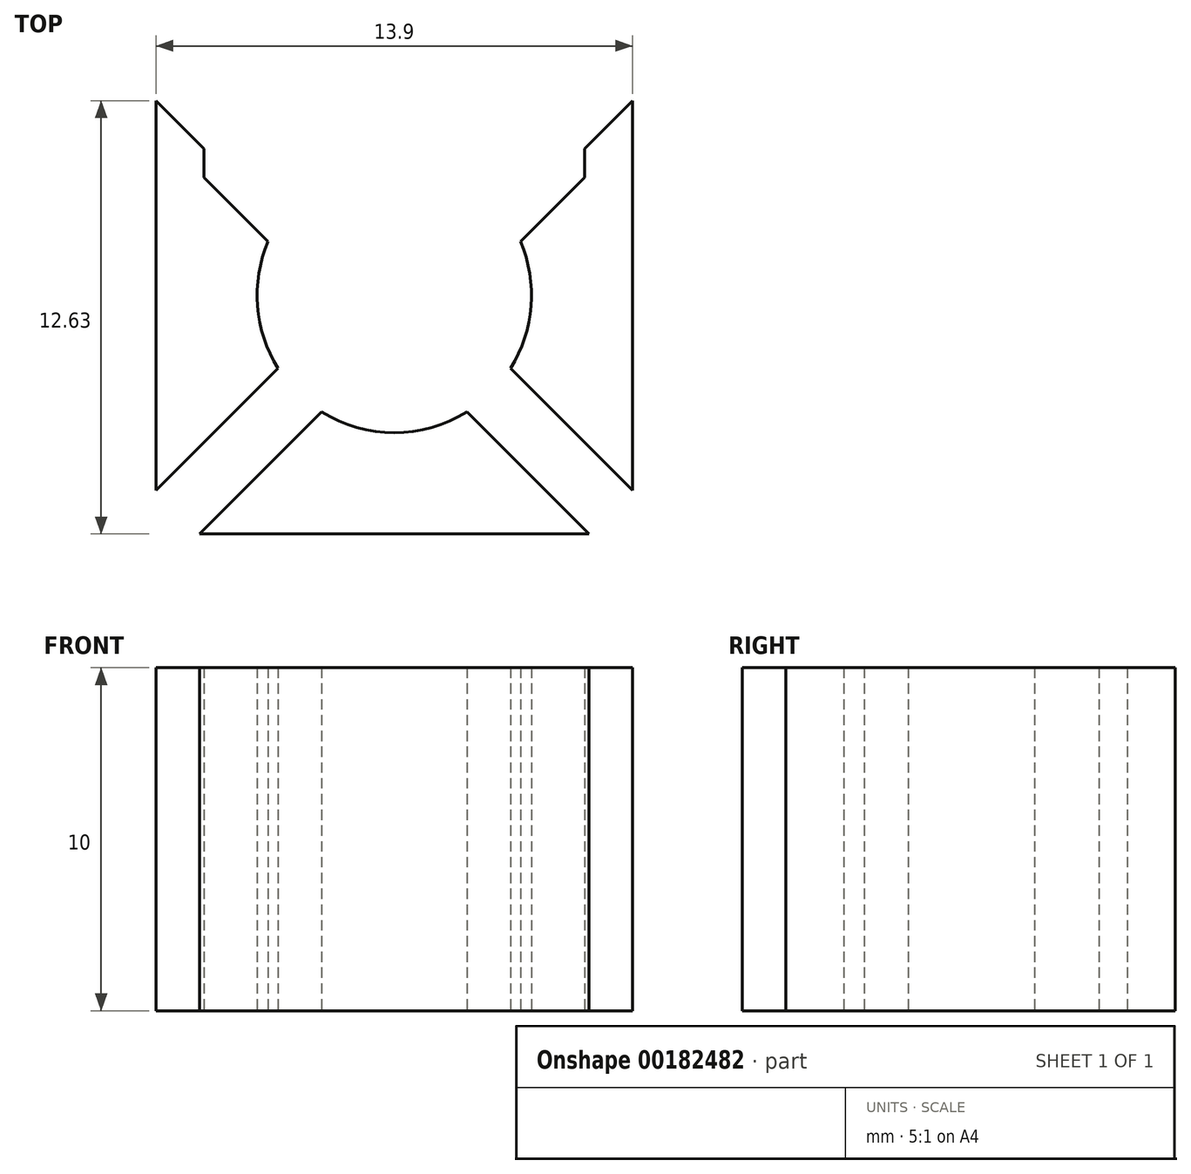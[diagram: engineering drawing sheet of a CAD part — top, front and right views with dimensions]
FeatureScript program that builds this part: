
annotation { "Feature Type Name" : "Feature", "Feature Type Description" : "" }
export const myFeature = defineFeature(function(context is Context, id is Id, definition is map)
    precondition{}
    {
        {
            var Q0;
            Q0=qCreatedBy(makeId("Top.planeOp"),FACE);
            var sketch = newSketch(context, id + "F0", { "sketchPlane" : qUnion([Q0])});
            skLineSegment(sketch, "E0.bottom", {"start": v(8.25, 8.25) * mm, "end": v(-8.25, 8.25) * mm});
            skLineSegment(sketch, "E0.top", {"start": v(8.25, -8.25) * mm, "end": v(-8.25, -8.25) * mm});
            skLineSegment(sketch, "E0.left", {"start": v(8.25, 8.25) * mm, "end": v(8.25, -8.25) * mm});
            skLineSegment(sketch, "E0.right", {"start": v(-8.25, 8.25) * mm, "end": v(-8.25, -8.25) * mm});
            skPoint(sketch, "E0.middle", {"position": v(0, 0) * mm});
            skLineSegment(sketch, "E1.0", {"start": v(7.45, 7.45) * mm, "end": v(-7.45, 7.45) * mm});
            skLineSegment(sketch, "E1.1", {"start": v(7.45, 7.45) * mm, "end": v(7.45, -7.45) * mm});
            skLineSegment(sketch, "E1.2", {"start": v(7.45, -7.45) * mm, "end": v(-7.45, -7.45) * mm});
            skLineSegment(sketch, "E1.3", {"start": v(-7.45, 7.45) * mm, "end": v(-7.45, -7.45) * mm});
            skLineSegment(sketch, "E2", {"start": v(4.25, 7.45) * mm, "end": v(5.05, 7.45) * mm});
            skLineSegment(sketch, "E3", {"start": v(5.05, 7.45) * mm, "end": v(5.05, 3.65) * mm});
            skLineSegment(sketch, "E4", {"start": v(5.05, 3.65) * mm, "end": v(-5.05, 3.65) * mm});
            skLineSegment(sketch, "E5", {"start": v(-5.05, 3.65) * mm, "end": v(-5.05, 7.45) * mm});
            skLineSegment(sketch, "E6", {"start": v(0, 4.45) * mm, "end": v(0, 7.45) * mm, "construction": true});
            skCircle(sketch, "E7", {"center": v(0, 0) * mm, "radius": 3.5 * mm});
            skLineSegment(sketch, "E8", {"start": v(-7.45, -7.45) * mm, "end": v(7.45, 7.45) * mm, "construction": true});
            skLineSegment(sketch, "E9", {"start": v(-7.45, 7.45) * mm, "end": v(7.45, -7.45) * mm, "construction": true});
            skLineSegment(sketch, "E10", {"start": v(-6.88, 7.45) * mm, "end": v(7.45, -6.88) * mm});
            skLineSegment(sketch, "E11", {"start": v(6.88, -7.45) * mm, "end": v(-7.45, 6.88) * mm});
            skLineSegment(sketch, "E12", {"start": v(6.88, 7.45) * mm, "end": v(-7.45, -6.88) * mm});
            skLineSegment(sketch, "E13", {"start": v(-6.88, -7.45) * mm, "end": v(7.45, 6.88) * mm});
            skLineSegment(sketch, "E14", {"start": v(-5.05, 3.65) * mm, "end": v(-3.07, 1.67) * mm});
            skLineSegment(sketch, "E15", {"start": v(5.05, 3.65) * mm, "end": v(3.07, 1.67) * mm});
            skLineSegment(sketch, "E16", {"start": v(-7.45, 6.88) * mm, "end": v(-5.05, 4.48) * mm});
            skSolve(sketch);
        }
        {
            var Q0;
            Q0=qCreatedBy(makeId("Top.planeOp"),FACE);
            var sketch = newSketch(context, id + "F1", { "sketchPlane" : qUnion([Q0])});
            skLineSegment(sketch, "E17.0", {"start": v(-5.55, 3.44) * mm, "end": v(-5.55, 4.28) * mm});
            skLineSegment(sketch, "E17.1", {"start": v(-6.95, 5.68) * mm, "end": v(-6.95, -5.68) * mm});
            skLineSegment(sketch, "E17.2", {"start": v(-6.95, -5.68) * mm, "end": v(-3.4, -2.12) * mm});
            skLineSegment(sketch, "E17.3", {"start": v(-5.55, 4.28) * mm, "end": v(-6.95, 5.68) * mm});
            skArc(sketch, "E17.4", {"start": v(-3.4, -2.12) * mm, "mid": v(-3.99, -0.3) * mm, "end": v(-3.68, 1.57) * mm});
            skLineSegment(sketch, "E17.5", {"start": v(-3.68, 1.57) * mm, "end": v(-5.55, 3.44) * mm});
            skLineSegment(sketch, "E18.0", {"start": v(6.95, 5.68) * mm, "end": v(5.55, 4.28) * mm});
            skLineSegment(sketch, "E18.1", {"start": v(5.55, 3.44) * mm, "end": v(3.68, 1.57) * mm});
            skArc(sketch, "E18.2", {"start": v(3.68, 1.57) * mm, "mid": v(3.99, -0.3) * mm, "end": v(3.4, -2.12) * mm});
            skLineSegment(sketch, "E18.3", {"start": v(5.55, 4.28) * mm, "end": v(5.55, 3.44) * mm});
            skLineSegment(sketch, "E18.4", {"start": v(3.4, -2.12) * mm, "end": v(6.95, -5.68) * mm});
            skLineSegment(sketch, "E18.5", {"start": v(6.95, -5.68) * mm, "end": v(6.95, 5.68) * mm});
            skLineSegment(sketch, "E19.0", {"start": v(-5.68, -6.95) * mm, "end": v(5.68, -6.95) * mm});
            skLineSegment(sketch, "E19.1", {"start": v(-2.12, -3.4) * mm, "end": v(-5.68, -6.95) * mm});
            skArc(sketch, "E19.2", {"start": v(2.12, -3.4) * mm, "mid": v(0, -4) * mm, "end": v(-2.12, -3.4) * mm});
            skLineSegment(sketch, "E19.3", {"start": v(5.68, -6.95) * mm, "end": v(2.12, -3.4) * mm});
            skSolve(sketch);
        }
        {
            var Q0;
            Q0 = qSketchRegion(id + "F1", true);
            extrude(context, id + "F2", {"entities" : qUnion([Q0]), "depth" : 10 * mm});
        }
    });
